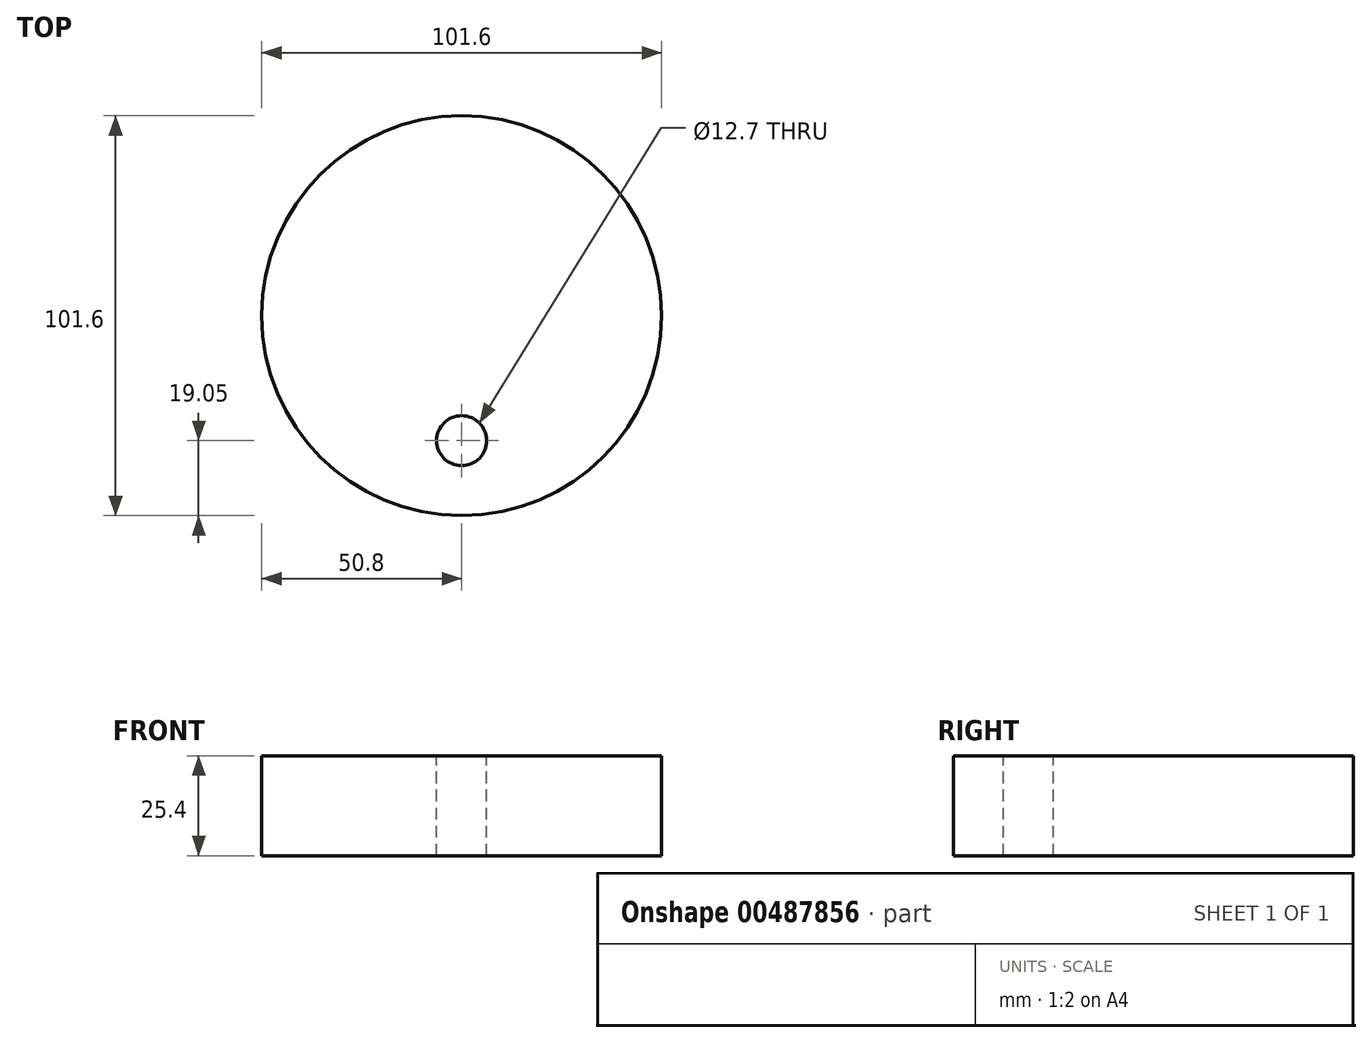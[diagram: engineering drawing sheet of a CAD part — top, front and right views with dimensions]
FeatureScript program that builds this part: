
annotation { "Feature Type Name" : "Feature", "Feature Type Description" : "" }
export const myFeature = defineFeature(function(context is Context, id is Id, definition is map)
    precondition{}
    {
        {
            var Q0;
            Q0=qCreatedBy(makeId("Top.planeOp"),FACE);
            var sketch = newSketch(context, id + "F0", { "sketchPlane" : qUnion([Q0])});
            skCircle(sketch, "E0", {"center": v(0, 0) * mm, "radius": 50.8 * mm});
            skSolve(sketch);
        }
        {
            var Q0;
            Q0 = qSketchRegion(id + "F0", true);
            extrude(context, id + "F1", {"entities" : qUnion([Q0]), "depth" : 25.4 * mm});
        }
        {
            var Q0;
            Q0=makeQuery(id+"F1.opExtrude","CAP_FACE",FACE,{"disambiguationData":[OSD([sQuery(id+"F0.wireOp",EDGE,"E0")])],"isStart":false});
            var sketch = newSketch(context, id + "F2", { "sketchPlane" : qUnion([Q0])});
            skCircle(sketch, "E1", {"center": v(0, 0) * mm, "radius": 31.75 * mm, "construction": true});
            skCircle(sketch, "E2", {"center": v(0, -31.75) * mm, "radius": 6.35 * mm});
            skSolve(sketch);
        }
        {
            var Q0;
            Q0=makeQuery(id+"F2.imprint","IMPRINT",FACE,{"disambiguationData":[TD([[makeQuery(id+"F2.imprint","IMPRINT",EDGE,{"derivedFrom":sQuery(id+"F2.wireOp",EDGE,"E2")}),1.0]])]});
            extrude(context, id + "F3", {"entities" : qUnion([Q0]), "operationType" : NewBodyOperationType.REMOVE, "endBound" : BoundingType.THROUGH_ALL, "oppositeDirection" : true, "depth" : 25.4 * mm});
        }
    });
